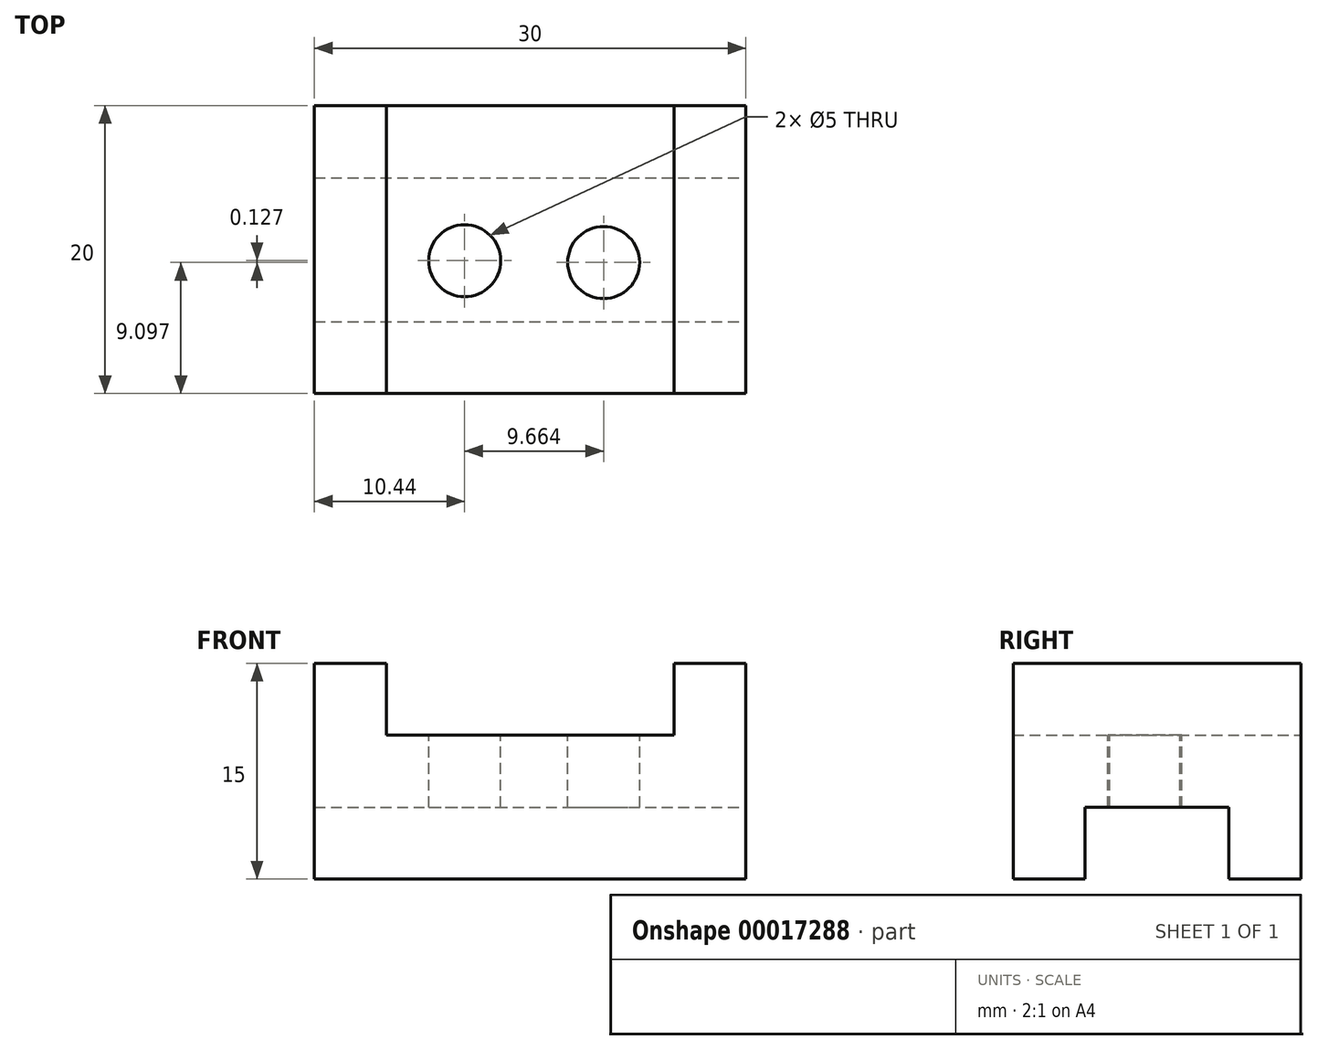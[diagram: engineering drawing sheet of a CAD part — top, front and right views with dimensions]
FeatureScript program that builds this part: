
annotation { "Feature Type Name" : "Feature", "Feature Type Description" : "" }
export const myFeature = defineFeature(function(context is Context, id is Id, definition is map)
    precondition{}
    {
        {
            var Q0;
            Q0=qCreatedBy(makeId("Front.planeOp"),FACE);
            var sketch = newSketch(context, id + "F0", { "sketchPlane" : qUnion([Q0])});
            skLineSegment(sketch, "E0.top", {"start": v(-30, -10) * mm, "end": v(0, -10) * mm});
            skLineSegment(sketch, "E0.left", {"start": v(-30, 0) * mm, "end": v(-30, -10) * mm});
            skLineSegment(sketch, "E0.right", {"start": v(0, 0) * mm, "end": v(0, -10) * mm});
            skLineSegment(sketch, "E1.top", {"start": v(-30, 5) * mm, "end": v(-25, 5) * mm});
            skLineSegment(sketch, "E1.left", {"start": v(-30, 0) * mm, "end": v(-30, 5) * mm});
            skLineSegment(sketch, "E1.right", {"start": v(-25, 0) * mm, "end": v(-25, 5) * mm});
            skLineSegment(sketch, "E2.top", {"start": v(0, 5) * mm, "end": v(-5, 5) * mm});
            skLineSegment(sketch, "E2.left", {"start": v(0, 0) * mm, "end": v(0, 5) * mm});
            skLineSegment(sketch, "E2.right", {"start": v(-5, 0) * mm, "end": v(-5, 5) * mm});
            skLineSegment(sketch, "E3", {"start": v(-25, 0) * mm, "end": v(-5, 0) * mm});
            skSolve(sketch);
        }
        {
            var Q0;
            Q0=makeQuery(id+"F0.imprint","IMPRINT",FACE,{"disambiguationData":[TD([[makeQuery(id+"F0.imprint","IMPRINT",EDGE,{"derivedFrom":sQuery(id+"F0.wireOp",EDGE,"E0.top")}),1.0]])]});
            extrude(context, id + "F1", {"entities" : qUnion([Q0]), "depth" : 20 * mm});
        }
        {
            var Q0;
            Q0=makeQuery(id+"F1.opExtrude","SWEPT_FACE",FACE,{"disambiguationData":[OSD([sQuery(id+"F0.wireOp",EDGE,"E0.right"),sQuery(id+"F0.wireOp",EDGE,"E2.left")])]});
            var sketch = newSketch(context, id + "F2", { "sketchPlane" : qUnion([Q0])});
            skLineSegment(sketch, "E4", {"start": v(-20, -10) * mm, "end": v(-15, -10) * mm});
            skLineSegment(sketch, "E5", {"start": v(-15, -10) * mm, "end": v(0, -10) * mm});
            skLineSegment(sketch, "E6", {"start": v(0, -10) * mm, "end": v(-5, -10) * mm});
            skLineSegment(sketch, "E7", {"start": v(-15, -10) * mm, "end": v(-15, -5) * mm});
            skLineSegment(sketch, "E8", {"start": v(-5, -10) * mm, "end": v(-5, -5) * mm});
            skLineSegment(sketch, "E9", {"start": v(-15, -5) * mm, "end": v(-5, -5) * mm});
            skSolve(sketch);
        }
        {
            var Q0;
            Q0=makeQuery(id+"F2.imprint","IMPRINT",FACE,{"disambiguationData":[TD([[makeQuery(id+"F2.imprint","IMPRINT",EDGE,{"derivedFrom":sQuery(id+"F2.wireOp",EDGE,"E5")}),1.0]])]});
            extrude(context, id + "F3", {"entities" : qUnion([Q0]), "operationType" : NewBodyOperationType.REMOVE, "oppositeDirection" : true, "depth" : 30 * mm});
        }
        {
            var Q0;
            Q0=makeQuery(id+"F1.opExtrude","SWEPT_FACE",FACE,{"disambiguationData":[OSD([sQuery(id+"F0.wireOp",EDGE,"E3")])]});
            var sketch = newSketch(context, id + "F4", { "sketchPlane" : qUnion([Q0])});
            skPoint(sketch, "E10", {"position": v(-15.7, -10.01) * mm});
            skPoint(sketch, "E11", {"position": v(-21.75, -10.01) * mm});
            skPoint(sketch, "E12", {"position": v(-8.23, -10.01) * mm});
            skSolve(sketch);
        }
        {
            var Q0;
            {var subQ0=sQuery(id+"F0.wireOp",EDGE,"E3");Q0=makeQuery(id+"F4.imprint","IMPRINT",FACE,{"disambiguationData":[TD([[makeQuery(id+"F4.imprint","IMPRINT",EDGE,{"derivedFrom":makeQuery(id+"F1.opExtrude","CAP_EDGE",EDGE,{"disambiguationData":[OSD([subQ0])],"isStart":true})}),-1.0]])]});}
            var sketch = newSketch(context, id + "F5", { "sketchPlane" : qUnion([Q0])});
            skLineSegment(sketch, "E13", {"start": v(-24.56, -19.94) * mm, "end": v(-19.56, -19.94) * mm});
            skLineSegment(sketch, "E14", {"start": v(-5.9, -19.95) * mm, "end": v(-10.9, -19.95) * mm});
            skPoint(sketch, "E15", {"position": v(-10.9, -10.78) * mm});
            skPoint(sketch, "E16", {"position": v(-19.56, -10.78) * mm});
            skSolve(sketch);
        }
        {
            var Q0;
            Q0=sQuery(id+"F5.wireOp",VERTEX,"E16");
            var Q1;
            Q1=makeQuery(id+"F1.opExtrude","SWEPT_BODY",BODY,{"disambiguationData":[OSD([sQuery(id+"F0.wireOp",EDGE,"E0.top"),sQuery(id+"F0.wireOp",EDGE,"E0.left"),sQuery(id+"F0.wireOp",EDGE,"E0.right"),sQuery(id+"F0.wireOp",EDGE,"E1.top"),sQuery(id+"F0.wireOp",EDGE,"E1.left"),sQuery(id+"F0.wireOp",EDGE,"E1.right"),sQuery(id+"F0.wireOp",EDGE,"E2.top"),sQuery(id+"F0.wireOp",EDGE,"E2.left"),sQuery(id+"F0.wireOp",EDGE,"E2.right"),sQuery(id+"F0.wireOp",EDGE,"E3")])]});
            hole(context, id + "F6", {"style" : HoleStyle.SIMPLE, "holeDiameter" : 5 * mm, "endStyle" : HoleEndStyle.THROUGH, "locations" : qUnion([Q0]), "scope" : qUnion([Q1])});
        }
        {
            var Q0;
            {var subQ0=sQuery(id+"F0.wireOp",EDGE,"E3");Q0=makeQuery(id+"F4.imprint","IMPRINT",FACE,{"disambiguationData":[TD([[makeQuery(id+"F4.imprint","IMPRINT",EDGE,{"derivedFrom":makeQuery(id+"F1.opExtrude","CAP_EDGE",EDGE,{"disambiguationData":[OSD([subQ0])],"isStart":true})}),-1.0]])]});}
            var sketch = newSketch(context, id + "F7", { "sketchPlane" : qUnion([Q0])});
            skLineSegment(sketch, "E17", {"start": v(-6.8, -19.83) * mm, "end": v(-11.8, -19.83) * mm});
            skPoint(sketch, "E18", {"position": v(-9.9, -10.9) * mm});
            skSolve(sketch);
        }
        {
            var Q0;
            Q0=sQuery(id+"F7.wireOp",VERTEX,"E18");
            var Q1;
            Q1=makeQuery(id+"F1.opExtrude","SWEPT_BODY",BODY,{"disambiguationData":[OSD([sQuery(id+"F0.wireOp",EDGE,"E0.top"),sQuery(id+"F0.wireOp",EDGE,"E0.left"),sQuery(id+"F0.wireOp",EDGE,"E0.right"),sQuery(id+"F0.wireOp",EDGE,"E1.top"),sQuery(id+"F0.wireOp",EDGE,"E1.left"),sQuery(id+"F0.wireOp",EDGE,"E1.right"),sQuery(id+"F0.wireOp",EDGE,"E2.top"),sQuery(id+"F0.wireOp",EDGE,"E2.left"),sQuery(id+"F0.wireOp",EDGE,"E2.right"),sQuery(id+"F0.wireOp",EDGE,"E3")])]});
            hole(context, id + "F8", {"style" : HoleStyle.SIMPLE, "holeDiameter" : 5 * mm, "endStyle" : HoleEndStyle.THROUGH, "locations" : qUnion([Q0]), "scope" : qUnion([Q1])});
        }
    });
